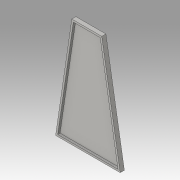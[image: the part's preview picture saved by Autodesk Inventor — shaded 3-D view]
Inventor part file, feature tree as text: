
AUTODESK INVENTOR PART (.ipt)
format: ipt  version: 2016 (Build 200138000, 138)  size: 83,968 bytes
history: native  units: in
note: dims shown in document units (in); Inventor stores cm internally (conversion verified against a paired STEP export)
features: extrude x1, shell x1, sketch x1
ambient origin geometry x8: Origin, YZ Plane, XZ Plane, XY Plane, X Axis, Y Axis, Z Axis, Center Point
bodies: Solid1 (feature_tree)
feature tree (3):
  extrude  "Extrusion1"  Depth=0.1in
  shell  "Shell1"  Thickness=0.225in
  sketch  "Sketch1"  dims[d0=3.5in d1=1.625in d2=0.225in d3=0.0in d4=0.1in]
